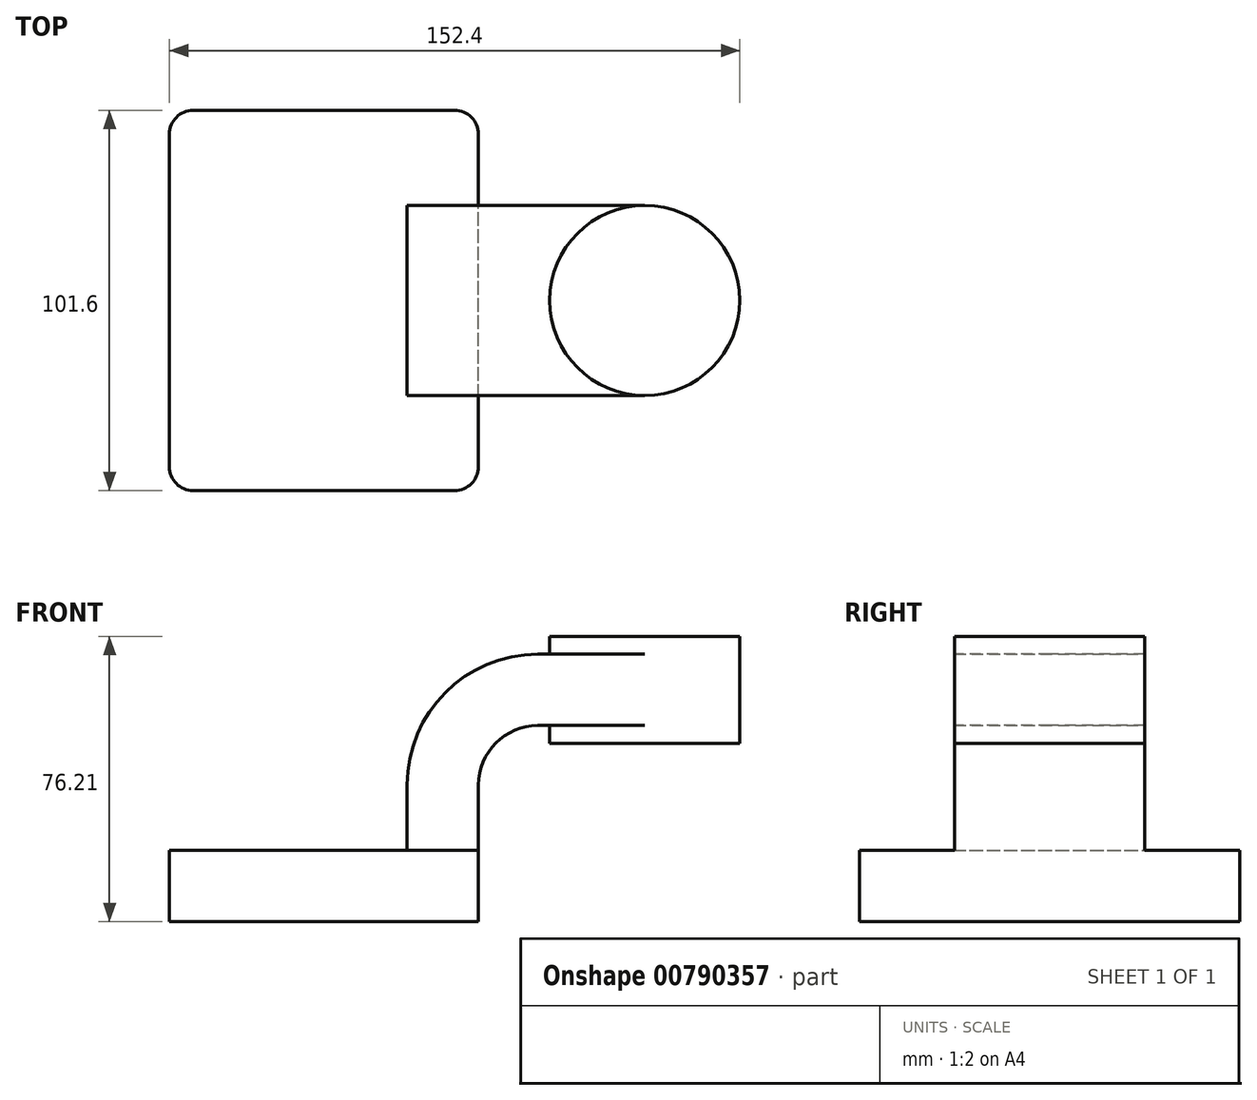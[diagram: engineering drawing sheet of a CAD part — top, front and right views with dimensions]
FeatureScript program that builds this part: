
annotation { "Feature Type Name" : "Feature", "Feature Type Description" : "" }
export const myFeature = defineFeature(function(context is Context, id is Id, definition is map)
    precondition{}
    {
        {
            var Q0;
            Q0=qCreatedBy(makeId("Front.planeOp"),FACE);
            var sketch = newSketch(context, id + "F0", { "sketchPlane" : qUnion([Q0])});
            skLineSegment(sketch, "E0.bottom", {"start": v(41.28, -9.52) * mm, "end": v(-41.28, -9.53) * mm});
            skLineSegment(sketch, "E0.top", {"start": v(41.28, 9.53) * mm, "end": v(-41.28, 9.53) * mm});
            skLineSegment(sketch, "E0.left", {"start": v(41.28, -9.52) * mm, "end": v(41.28, 9.53) * mm});
            skLineSegment(sketch, "E0.right", {"start": v(-41.28, -9.53) * mm, "end": v(-41.28, 9.53) * mm});
            skPoint(sketch, "E0.middle", {"position": v(0, 0) * mm});
            skLineSegment(sketch, "E1.bottom", {"start": v(111.12, 38.1) * mm, "end": v(60.32, 38.1) * mm});
            skLineSegment(sketch, "E1.top", {"start": v(111.12, 66.68) * mm, "end": v(60.32, 66.68) * mm});
            skLineSegment(sketch, "E1.left", {"start": v(111.12, 38.1) * mm, "end": v(111.12, 66.68) * mm});
            skLineSegment(sketch, "E1.right", {"start": v(60.32, 38.1) * mm, "end": v(60.32, 66.68) * mm});
            skPoint(sketch, "E1.middle", {"position": v(85.72, 52.39) * mm});
            skLineSegment(sketch, "E2", {"start": v(41.28, 9.53) * mm, "end": v(41.28, 27) * mm});
            skArc(sketch, "E3", {"start": v(41.27, 27) * mm, "mid": v(45.92, 38.23) * mm, "end": v(57.15, 42.88) * mm});
            skLineSegment(sketch, "E4", {"start": v(57.15, 42.88) * mm, "end": v(60.32, 42.88) * mm});
            skLineSegment(sketch, "E5.0", {"start": v(57.15, 61.93) * mm, "end": v(60.32, 61.93) * mm});
            skArc(sketch, "E5.1", {"start": v(22.23, 27) * mm, "mid": v(32.45, 51.7) * mm, "end": v(57.15, 61.93) * mm});
            skLineSegment(sketch, "E5.2", {"start": v(22.22, 9.53) * mm, "end": v(22.22, 27) * mm});
            skFitSpline(sketch, "E6", {"points": [v(-41.28, 9.52) * mm, v(57.15, 61.93) * mm], "startDerivative": vector(71.2, 76.38) * mm, "endDerivative": vector(120.05, -4.13) * mm});
            skLineSegment(sketch, "E7", {"start": v(60.32, 61.93) * mm, "end": v(85.72, 61.93) * mm});
            skLineSegment(sketch, "E8", {"start": v(60.32, 42.88) * mm, "end": v(85.72, 42.88) * mm});
            skLineSegment(sketch, "E9", {"start": v(85.72, 38.1) * mm, "end": v(85.72, 66.68) * mm});
            skPoint(sketch, "E9.startSnap0", {"position": v(85.72, 38.1) * mm});
            skPoint(sketch, "E10.orphan", {"position": v(92.14, 61.93) * mm});
            skPoint(sketch, "E11.orphan", {"position": v(93.53, 42.88) * mm});
            skSolve(sketch);
        }
        {
            var Q0;
            Q0=makeQuery(id+"F0.imprint","IMPRINT",FACE,{"disambiguationData":[TD([[makeQuery(id+"F0.imprint","IMPRINT",EDGE,{"derivedFrom":sQuery(id+"F0.wireOp",EDGE,"E0.bottom")}),-1.0]])]});
            extrude(context, id + "F1", {"entities" : qUnion([Q0]), "endBound" : BoundingType.SYMMETRIC, "depth" : 101.6 * mm, "offsetDistance" : 25.4 * mm});
        }
        {
            var Q0;
            {var subQ0=sQuery(id+"F0.wireOp",EDGE,"E2");Q0=makeQuery(id+"F0.imprint","IMPRINT",FACE,{"disambiguationData":[TD([[makeQuery(id+"F0.imprint","IMPRINT",EDGE,{"derivedFrom":subQ0}),1.0]])]});}
            var Q1;
            {var subQ2=sQuery(id+"F0.wireOp",EDGE,"E7");Q1=makeQuery(id+"F0.imprint","IMPRINT",FACE,{"disambiguationData":[TD([[makeQuery(id+"F0.imprint","IMPRINT",EDGE,{"derivedFrom":subQ2}),-1.0]])]});}
            extrude(context, id + "F2", {"entities" : qUnion([Q0, Q1]), "operationType" : NewBodyOperationType.ADD, "endBound" : BoundingType.SYMMETRIC, "depth" : 50.8 * mm, "offsetDistance" : 25.4 * mm});
        }
        {
            var Q0;
            Q0=makeQuery(id+"F0.imprint","IMPRINT",FACE,{"disambiguationData":[TD([[makeQuery(id+"F0.imprint","IMPRINT",EDGE,{"derivedFrom":sQuery(id+"F0.wireOp",EDGE,"E5.1")}),1.0]])]});
            extrude(context, id + "F3", {"entities" : qUnion([Q0]), "operationType" : NewBodyOperationType.ADD, "endBound" : BoundingType.SYMMETRIC, "depth" : 15.88 * mm, "offsetDistance" : 25.4 * mm});
        }
        {
            var Q0;
            {var subQ0=sQuery(id+"F0.wireOp",EDGE,"E1.left");Q0=makeQuery(id+"F0.imprint","IMPRINT",FACE,{"disambiguationData":[TD([[makeQuery(id+"F0.imprint","IMPRINT",EDGE,{"derivedFrom":subQ0}),1.0]])]});}
            var Q1;
            Q1=sQuery(id+"F0.wireOp",EDGE,"E9");
            revolve(context, id + "F4", {"operationType" : NewBodyOperationType.ADD, "surfaceOperationType" : NewSurfaceOperationType.NEW, "entities" : qUnion([Q0]), "axis" : qUnion([Q1]), "revolveType" : RevolveType.FULL});
        }
        {
            var Q0;
            Q0=makeQuery(id+"F1.opExtrude","CAP_EDGE",EDGE,{"disambiguationData":[OSD([sQuery(id+"F0.wireOp",EDGE,"E0.right")])],"isStart":false});
            var Q1;
            Q1=makeQuery(id+"F1.opExtrude","CAP_EDGE",EDGE,{"disambiguationData":[OSD([sQuery(id+"F0.wireOp",EDGE,"E0.left")])],"isStart":false});
            var Q2;
            Q2=makeQuery(id+"F1.opExtrude","CAP_EDGE",EDGE,{"disambiguationData":[OSD([sQuery(id+"F0.wireOp",EDGE,"E0.left")])],"isStart":true});
            var Q3;
            Q3=makeQuery(id+"F1.opExtrude","CAP_EDGE",EDGE,{"disambiguationData":[OSD([sQuery(id+"F0.wireOp",EDGE,"E0.right")])],"isStart":true});
            fillet(context, id + "F5", {"entities" : qUnion([Q0, Q1, Q2, Q3]), "radius" : 6.35 * mm, "tangentPropagation" : true, "allowEdgeOverflow" : false});
        }
    });
